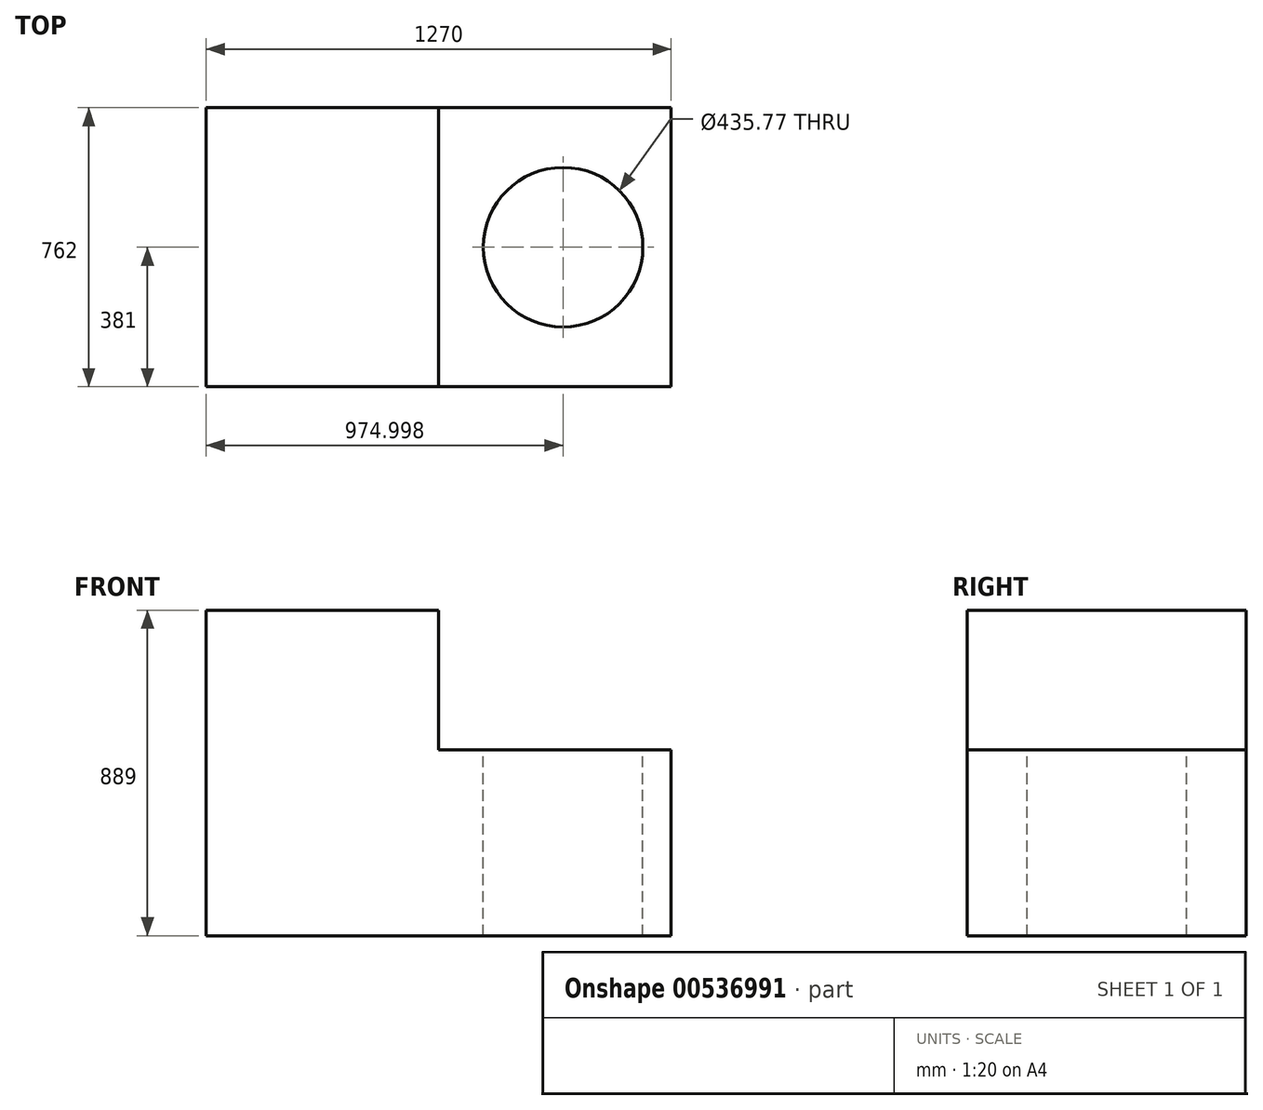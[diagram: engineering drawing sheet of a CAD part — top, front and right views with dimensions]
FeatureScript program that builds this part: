
annotation { "Feature Type Name" : "Feature", "Feature Type Description" : "" }
export const myFeature = defineFeature(function(context is Context, id is Id, definition is map)
    precondition{}
    {
        {
            var Q0;
            Q0=qCreatedBy(makeId("Front.planeOp"),FACE);
            var sketch = newSketch(context, id + "F0", { "sketchPlane" : qUnion([Q0])});
            skLineSegment(sketch, "E0", {"start": v(0, 0) * mm, "end": v(-1270, 0) * mm});
            skLineSegment(sketch, "E1", {"start": v(-1270, 0) * mm, "end": v(-1270, 889) * mm});
            skLineSegment(sketch, "E2", {"start": v(-1270, 889) * mm, "end": v(-635, 889) * mm});
            skLineSegment(sketch, "E3", {"start": v(-635, 889) * mm, "end": v(-635, 508) * mm});
            skLineSegment(sketch, "E4", {"start": v(-635, 508) * mm, "end": v(0, 508) * mm});
            skLineSegment(sketch, "E5", {"start": v(0, 508) * mm, "end": v(0, 0) * mm});
            skSolve(sketch);
        }
        {
            var Q0;
            Q0=makeQuery(id+"F0.imprint","IMPRINT",FACE,{"disambiguationData":[TD([[makeQuery(id+"F0.imprint","IMPRINT",EDGE,{"derivedFrom":sQuery(id+"F0.wireOp",EDGE,"E0")}),-1.0]])]});
            var Q1;
            Q1 = qSketchRegion(id + "F2", true);
            extrude(context, id + "F1", {"entities" : qUnion([Q0, Q1]), "depth" : 762 * mm, "offsetDistance" : 25.4 * mm});
        }
        {
            var Q0;
            Q0=makeQuery(id+"F1.opExtrude","SWEPT_FACE",FACE,{"disambiguationData":[OSD([sQuery(id+"F0.wireOp",EDGE,"E4")])]});
            var sketch = newSketch(context, id + "F2", { "sketchPlane" : qUnion([Q0])});
            skCircle(sketch, "E6", {"center": v(-295, -381) * mm, "radius": 217.89 * mm});
            skPoint(sketch, "E6.centerSnap0", {"position": v(0, -381) * mm});
            skSolve(sketch);
        }
        {
            var Q0;
            Q0=makeQuery(id+"F2.imprint","IMPRINT",FACE,{"disambiguationData":[TD([[makeQuery(id+"F2.imprint","IMPRINT",EDGE,{"derivedFrom":sQuery(id+"F2.wireOp",EDGE,"E6")}),1.0]])]});
            extrude(context, id + "F3", {"entities" : qUnion([Q0]), "operationType" : NewBodyOperationType.REMOVE, "oppositeDirection" : true, "depth" : 508 * mm, "offsetDistance" : 25.4 * mm});
        }
    });
